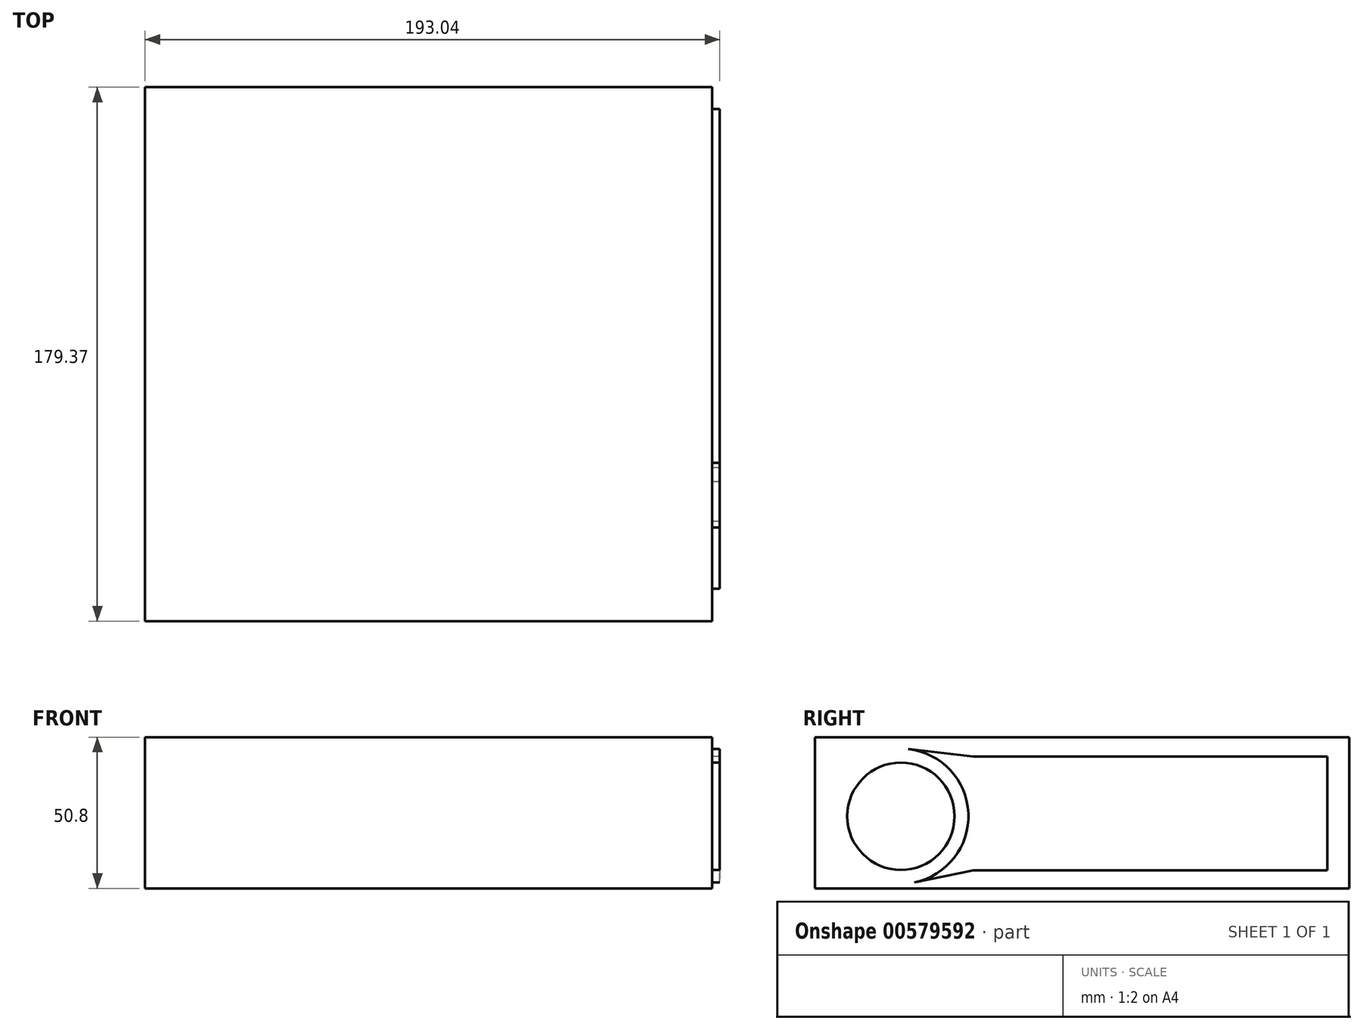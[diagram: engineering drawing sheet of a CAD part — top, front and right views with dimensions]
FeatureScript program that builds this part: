
annotation { "Feature Type Name" : "Feature", "Feature Type Description" : "" }
export const myFeature = defineFeature(function(context is Context, id is Id, definition is map)
    precondition{}
    {
        {
            var Q0;
            Q0=qCreatedBy(makeId("Front.planeOp"),FACE);
            var sketch = newSketch(context, id + "F0", { "sketchPlane" : qUnion([Q0])});
            skLineSegment(sketch, "E0.bottom", {"start": v(0, 0) * mm, "end": v(190.5, 0) * mm});
            skLineSegment(sketch, "E0.top", {"start": v(0, 50.8) * mm, "end": v(190.5, 50.8) * mm});
            skLineSegment(sketch, "E0.left", {"start": v(0, 0) * mm, "end": v(0, 50.8) * mm});
            skLineSegment(sketch, "E0.right", {"start": v(190.5, 0) * mm, "end": v(190.5, 50.8) * mm});
            skSolve(sketch);
        }
        {
            var Q0;
            Q0 = qSketchRegion(id + "F0", true);
            extrude(context, id + "F1", {"entities" : qUnion([Q0]), "oppositeDirection" : true, "depth" : 179.37 * mm, "offsetDistance" : 25.4 * mm});
        }
        {
            var Q0;
            Q0=makeQuery(id+"F1.opExtrude","SWEPT_FACE",FACE,{"disambiguationData":[OSD([sQuery(id+"F0.wireOp",EDGE,"E0.right")])]});
            var sketch = newSketch(context, id + "F2", { "sketchPlane" : qUnion([Q0])});
            skCircle(sketch, "E1", {"center": v(28.83, 24.22) * mm, "radius": 18.03 * mm});
            skLineSegment(sketch, "E2.bottom", {"start": v(51.85, 42.21) * mm, "end": v(172.8, 42.21) * mm});
            skLineSegment(sketch, "E2.top", {"start": v(51.85, 8.34) * mm, "end": v(172.8, 8.34) * mm});
            skLineSegment(sketch, "E2.left", {"start": v(51.85, 42.21) * mm, "end": v(51.85, 8.34) * mm});
            skLineSegment(sketch, "E2.right", {"start": v(172.8, 42.21) * mm, "end": v(172.8, 8.34) * mm});
            skSolve(sketch);
        }
        {
            var Q0;
            Q0=makeQuery(id+"F2.imprint","IMPRINT",FACE,{"disambiguationData":[TD([[makeQuery(id+"F2.imprint","IMPRINT",EDGE,{"derivedFrom":sQuery(id+"F2.wireOp",EDGE,"E1")}),1.0]])]});
            extrude(context, id + "F3", {"entities" : qUnion([Q0]), "operationType" : NewBodyOperationType.ADD, "depth" : 2.54 * mm, "offsetDistance" : 25.4 * mm});
        }
        {
            var Q0;
            Q0=makeQuery(id+"F1.opExtrude","SWEPT_FACE",FACE,{"disambiguationData":[OSD([sQuery(id+"F0.wireOp",EDGE,"E0.right")])]});
            var sketch = newSketch(context, id + "F4", { "sketchPlane" : qUnion([Q0])});
            skArc(sketch, "E3", {"start": v(33.42, 2) * mm, "mid": v(51.5, 25.24) * mm, "end": v(31.4, 46.76) * mm});
            skLineSegment(sketch, "E4.bottom", {"start": v(53.2, 44.28) * mm, "end": v(172.03, 44.28) * mm});
            skLineSegment(sketch, "E4.top", {"start": v(53.2, 6.08) * mm, "end": v(172.03, 6.08) * mm});
            skLineSegment(sketch, "E4.right", {"start": v(172.03, 44.28) * mm, "end": v(172.03, 6.08) * mm});
            skLineSegment(sketch, "E5", {"start": v(53.2, 44.28) * mm, "end": v(31.4, 46.76) * mm});
            skLineSegment(sketch, "E6", {"start": v(53.2, 6.08) * mm, "end": v(33.42, 2) * mm});
            skSolve(sketch);
        }
        {
            var Q0;
            Q0=makeQuery(id+"F4.imprint","IMPRINT",FACE,{"disambiguationData":[TD([[makeQuery(id+"F4.imprint","IMPRINT",EDGE,{"derivedFrom":sQuery(id+"F4.wireOp",EDGE,"E3")}),-1.0]])]});
            extrude(context, id + "F5", {"entities" : qUnion([Q0]), "operationType" : NewBodyOperationType.ADD, "depth" : 2.54 * mm, "offsetDistance" : 25.4 * mm});
        }
    });
